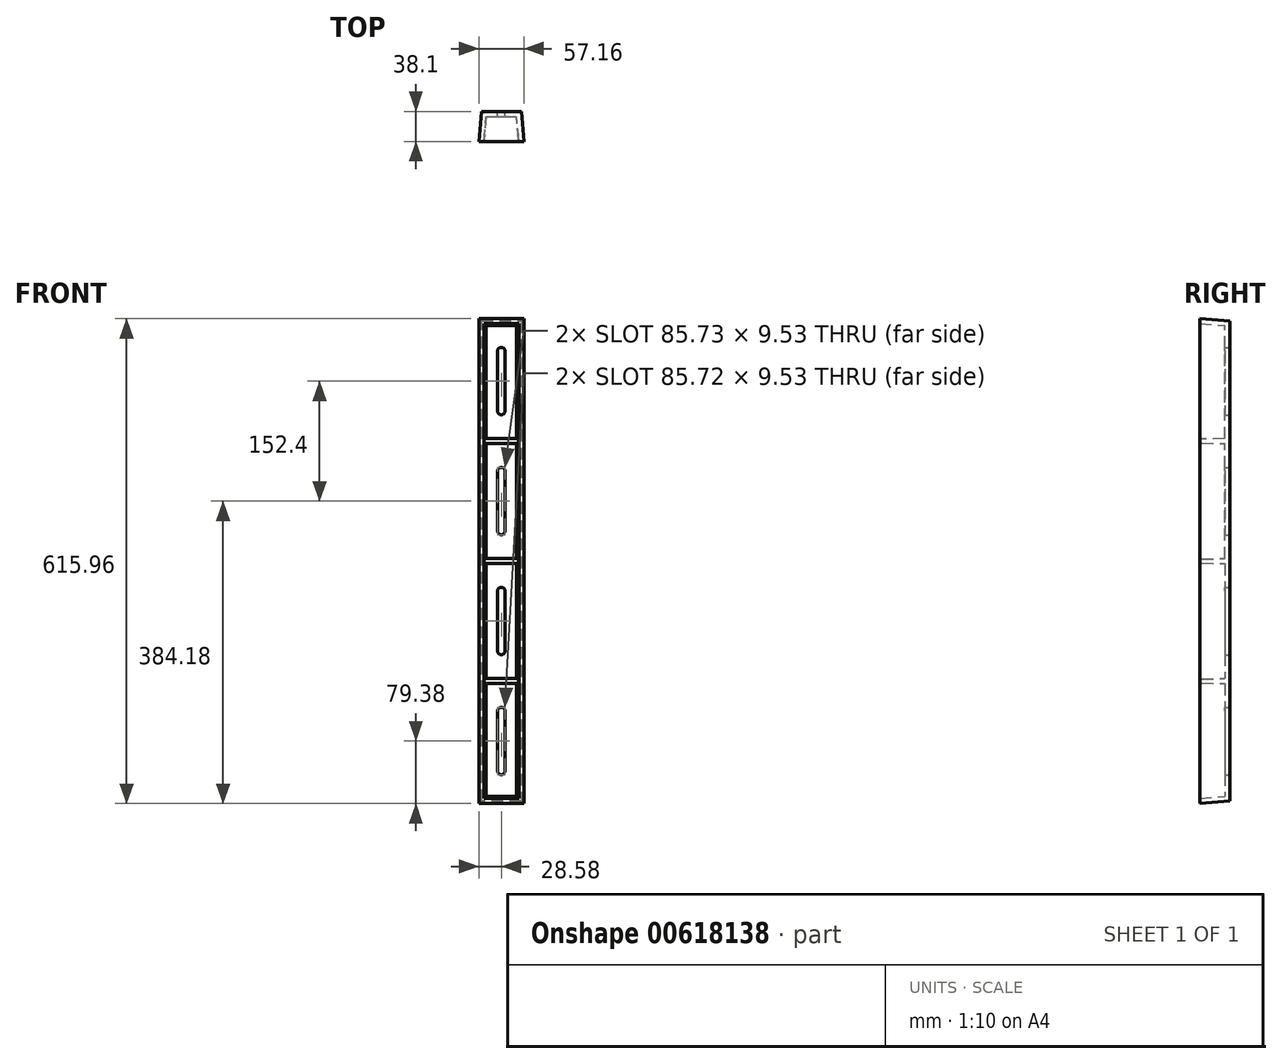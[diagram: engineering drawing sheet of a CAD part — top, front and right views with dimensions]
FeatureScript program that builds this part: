
annotation { "Feature Type Name" : "Feature", "Feature Type Description" : "" }
export const myFeature = defineFeature(function(context is Context, id is Id, definition is map)
    precondition{}
    {
        {
            var Q0;
            Q0=qCreatedBy(makeId("Front.planeOp"),FACE);
            var sketch = newSketch(context, id + "F0", { "sketchPlane" : qUnion([Q0])});
            skLineSegment(sketch, "E0.bottom", {"start": v(0, 0) * mm, "end": v(50.8, 0) * mm});
            skLineSegment(sketch, "E0.top", {"start": v(0, 609.6) * mm, "end": v(50.8, 609.6) * mm});
            skLineSegment(sketch, "E0.left", {"start": v(0, 0) * mm, "end": v(0, 609.6) * mm});
            skLineSegment(sketch, "E0.right", {"start": v(50.8, 0) * mm, "end": v(50.8, 609.6) * mm});
            skSolve(sketch);
        }
        {
            var Q0;
            Q0=qSketchRegion(id+"F0",true);
            extrude(context, id + "F1", {"entities" : qUnion([Q0]), "depth" : 38.1 * mm, "hasDraft" : true, "draftAngle" : 4.76 * degree});
        }
        {
            var Q0;
            Q0=makeQuery(id+"F1.opExtrude","CAP_FACE",FACE,{"disambiguationData":[OSD([sQuery(id+"F0.wireOp",EDGE,"E0.bottom"),sQuery(id+"F0.wireOp",EDGE,"E0.top"),sQuery(id+"F0.wireOp",EDGE,"E0.left"),sQuery(id+"F0.wireOp",EDGE,"E0.right")])],"isStart":false});
            shell(context, id + "F2", {"entities" : qUnion([Q0]), "thickness" : 6.35 * mm});
        }
        {
            var Q0;
            Q0=makeQuery(id+"F1.opExtrude","CAP_FACE",FACE,{"disambiguationData":[OSD([sQuery(id+"F0.wireOp",EDGE,"E0.bottom"),sQuery(id+"F0.wireOp",EDGE,"E0.top"),sQuery(id+"F0.wireOp",EDGE,"E0.left"),sQuery(id+"F0.wireOp",EDGE,"E0.right")])],"isStart":true});
            var sketch = newSketch(context, id + "F3", { "sketchPlane" : qUnion([Q0])});
            skLineSegment(sketch, "E1", {"start": v(-25.4, 0) * mm, "end": v(-25.4, 152.4) * mm, "construction": true});
            skLineSegment(sketch, "E2", {"start": v(-25.4, 152.4) * mm, "end": v(-25.4, 304.8) * mm, "construction": true});
            skLineSegment(sketch, "E3", {"start": v(-25.4, 304.8) * mm, "end": v(-25.4, 457.2) * mm, "construction": true});
            skLineSegment(sketch, "E4", {"start": v(-25.4, 457.2) * mm, "end": v(-25.4, 609.6) * mm, "construction": true});
            skSolve(sketch);
        }
        {
            var Q0;
            Q0=makeQuery(id+"F1.opExtrude","CAP_EDGE",EDGE,{"disambiguationData":[OSD([sQuery(id+"F0.wireOp",EDGE,"E0.bottom")])],"isStart":true});
            cPoint(context, id + "F4", {"entities" : qUnion([Q0]), "parameter" : 0.5});
        }
        {
            var Q0;
            Q0=makeQuery(id+"F1.opExtrude","CAP_EDGE",EDGE,{"disambiguationData":[OSD([sQuery(id+"F0.wireOp",EDGE,"E0.bottom")])],"isStart":false});
            cPoint(context, id + "F5", {"entities" : qUnion([Q0]), "parameter" : 0.5});
        }
        {
            var Q0;
            {var subQ0=sQuery(id+"F0.wireOp",EDGE,"E0.top");Q0=makeQuery(id+"F2.opShell","OFFSET_EDGE",EDGE,{"disambiguationData":[OSD([subQ0]),TDD([makeQuery(id+"F1.opExtrude","CAP_EDGE",EDGE,{"disambiguationData":[OSD([subQ0])],"isStart":false})])]});}
            cPoint(context, id + "F6", {"entities" : qUnion([Q0]), "parameter" : 0.5});
        }
        {
            var Q0;
            Q0=qCreatedBy(id+"F4",VERTEX);
            var Q1;
            Q1=qCreatedBy(id+"F5",VERTEX);
            var Q2;
            Q2=qCreatedBy(id+"F6",VERTEX);
            cPlane(context, id + "F7", {"entities" : qUnion([Q0, Q1, Q2]), "cplaneType" : CPlaneType.THREE_POINT, "offset" : 25.4 * mm, "width" : 152.4 * mm, "height" : 152.4 * mm});
        }
        {
            var Q0;
            Q0=qCreatedBy(id+"F7.planeOp",FACE);
            var sketch = newSketch(context, id + "F8", { "sketchPlane" : qUnion([Q0])});
            skLineSegment(sketch, "E5", {"start": v(-6.35, 603.76) * mm, "end": v(-6.35, 5.84) * mm});
            skLineSegment(sketch, "E6.0", {"start": v(0, 152.4) * mm, "end": v(0, 304.8) * mm, "construction": true});
            skLineSegment(sketch, "E7.0", {"start": v(0, 0) * mm, "end": v(0, 152.4) * mm});
            skLineSegment(sketch, "E8.0", {"start": v(0, 304.8) * mm, "end": v(0, 457.2) * mm, "construction": true});
            skLineSegment(sketch, "E9.0", {"start": v(0, 457.2) * mm, "end": v(0, 609.6) * mm, "construction": true});
            skLineSegment(sketch, "E10.0.0", {"start": v(-6.35, 5.84) * mm, "end": v(-6.35, 603.76) * mm});
            skLineSegment(sketch, "E10.0.1", {"start": v(-6.35, 603.76) * mm, "end": v(-38.1, 606.4) * mm});
            skLineSegment(sketch, "E10.0.2", {"start": v(-38.1, 606.4) * mm, "end": v(-38.1, 3.2) * mm, "construction": true});
            skLineSegment(sketch, "E10.0.3", {"start": v(-38.1, 3.2) * mm, "end": v(-6.35, 5.84) * mm});
            skLineSegment(sketch, "E11", {"start": v(0, 152.4) * mm, "end": v(-38.1, 152.4) * mm, "construction": true});
            skLineSegment(sketch, "E12", {"start": v(0, 304.8) * mm, "end": v(-38.1, 304.8) * mm, "construction": true});
            skLineSegment(sketch, "E13", {"start": v(0, 457.2) * mm, "end": v(-38.1, 457.2) * mm, "construction": true});
            skLineSegment(sketch, "E14.0", {"start": v(0, 155.58) * mm, "end": v(-6.35, 155.58) * mm, "construction": true});
            skLineSegment(sketch, "E15.0", {"start": v(0, 149.22) * mm, "end": v(-6.35, 149.22) * mm, "construction": true});
            skLineSegment(sketch, "E16.0", {"start": v(0, 301.63) * mm, "end": v(-6.35, 301.63) * mm, "construction": true});
            skLineSegment(sketch, "E17.0", {"start": v(0, 307.98) * mm, "end": v(-6.35, 307.98) * mm, "construction": true});
            skLineSegment(sketch, "E18.0", {"start": v(0, 460.38) * mm, "end": v(-6.35, 460.38) * mm, "construction": true});
            skLineSegment(sketch, "E19.0", {"start": v(0, 454.03) * mm, "end": v(-6.35, 454.03) * mm, "construction": true});
            skArc(sketch, "E20", {"start": v(-35.78, 154.78) * mm, "mid": v(-38.1, 152.4) * mm, "end": v(-35.78, 150.02) * mm});
            skArc(sketch, "E21", {"start": v(-35.78, 307.18) * mm, "mid": v(-38.1, 304.8) * mm, "end": v(-35.78, 302.42) * mm});
            skArc(sketch, "E22", {"start": v(-35.78, 459.58) * mm, "mid": v(-38.1, 457.2) * mm, "end": v(-35.78, 454.82) * mm});
            skLineSegment(sketch, "E23", {"start": v(-6.35, 149.22) * mm, "end": v(-35.78, 150.02) * mm});
            skLineSegment(sketch, "E24", {"start": v(-6.35, 155.57) * mm, "end": v(-35.78, 154.78) * mm});
            skLineSegment(sketch, "E25", {"start": v(-6.35, 301.63) * mm, "end": v(-35.78, 302.42) * mm});
            skLineSegment(sketch, "E26", {"start": v(-6.35, 307.98) * mm, "end": v(-35.78, 307.18) * mm});
            skLineSegment(sketch, "E27", {"start": v(-6.35, 454.03) * mm, "end": v(-35.78, 454.82) * mm});
            skLineSegment(sketch, "E28", {"start": v(-6.35, 460.38) * mm, "end": v(-35.78, 459.58) * mm});
            skSolve(sketch);
        }
        {
            var Q0;
            Q0=qSketchRegion(id+"F8",true);
            var Q1;
            Q1=makeQuery(id+"F2.opShell","OFFSET_FACE",FACE,{"disambiguationData":[OSD([sQuery(id+"F0.wireOp",EDGE,"E0.left")])]});
            var Q2;
            Q2=makeQuery(id+"F2.opShell","OFFSET_FACE",FACE,{"disambiguationData":[OSD([sQuery(id+"F0.wireOp",EDGE,"E0.right")])]});
            extrude(context, id + "F9", {"entities" : qUnion([Q0]), "operationType" : NewBodyOperationType.ADD, "endBound" : BoundingType.UP_TO_SURFACE, "oppositeDirection" : true, "endBoundEntityFace" : qUnion([Q1]), "depth" : 25.4 * mm, "hasSecondDirection" : true, "secondDirectionBound" : SecondDirectionBoundingType.UP_TO_SURFACE, "secondDirectionOppositeDirection" : false, "secondDirectionBoundEntityFace" : qUnion([Q2]), "secondDirectionDepth" : 25.4 * mm});
        }
        {
            var Q0;
            Q0=makeQuery(id+"F3.imprint","IMPRINT",FACE,{"disambiguationData":[TD([[makeQuery(id+"F3.imprint","IMPRINT",EDGE,{"derivedFrom":makeQuery(id+"F1.opExtrude","CAP_EDGE",EDGE,{"disambiguationData":[OSD([sQuery(id+"F0.wireOp",EDGE,"E0.bottom")])],"isStart":true})}),-1.0]])]});
            var sketch = newSketch(context, id + "F10", { "sketchPlane" : qUnion([Q0])});
            skLineSegment(sketch, "E29.0", {"start": v(-25.4, 457.2) * mm, "end": v(-25.4, 609.6) * mm, "construction": true});
            skLineSegment(sketch, "E30.0", {"start": v(-25.4, 304.8) * mm, "end": v(-25.4, 457.2) * mm, "construction": true});
            skLineSegment(sketch, "E31.0", {"start": v(-25.4, 152.4) * mm, "end": v(-25.4, 304.8) * mm, "construction": true});
            skLineSegment(sketch, "E32.0", {"start": v(-25.4, 0) * mm, "end": v(-25.4, 152.4) * mm, "construction": true});
            skLineSegment(sketch, "E33.bottom", {"start": v(-30.16, 495.3) * mm, "end": v(-20.64, 495.3) * mm});
            skLineSegment(sketch, "E33.top", {"start": v(-30.16, 571.5) * mm, "end": v(-20.64, 571.5) * mm});
            skLineSegment(sketch, "E33.left", {"start": v(-30.16, 495.3) * mm, "end": v(-30.16, 571.5) * mm});
            skLineSegment(sketch, "E33.right", {"start": v(-20.64, 495.3) * mm, "end": v(-20.64, 571.5) * mm});
            skPoint(sketch, "E33.middle", {"position": v(-25.4, 533.4) * mm});
            skLineSegment(sketch, "E34.bottom", {"start": v(-30.16, 342.9) * mm, "end": v(-20.64, 342.9) * mm});
            skLineSegment(sketch, "E34.top", {"start": v(-30.16, 419.1) * mm, "end": v(-20.64, 419.1) * mm});
            skLineSegment(sketch, "E34.left", {"start": v(-30.16, 342.9) * mm, "end": v(-30.16, 419.1) * mm});
            skLineSegment(sketch, "E34.right", {"start": v(-20.64, 342.9) * mm, "end": v(-20.64, 419.1) * mm});
            skPoint(sketch, "E34.middle", {"position": v(-25.4, 381) * mm});
            skLineSegment(sketch, "E35.bottom", {"start": v(-30.16, 190.5) * mm, "end": v(-20.64, 190.5) * mm});
            skLineSegment(sketch, "E35.top", {"start": v(-30.16, 266.7) * mm, "end": v(-20.64, 266.7) * mm});
            skLineSegment(sketch, "E35.left", {"start": v(-30.16, 190.5) * mm, "end": v(-30.16, 266.7) * mm});
            skLineSegment(sketch, "E35.right", {"start": v(-20.64, 190.5) * mm, "end": v(-20.64, 266.7) * mm});
            skPoint(sketch, "E35.middle", {"position": v(-25.4, 228.6) * mm});
            skLineSegment(sketch, "E36.bottom", {"start": v(-30.16, 38.1) * mm, "end": v(-20.64, 38.1) * mm});
            skLineSegment(sketch, "E36.top", {"start": v(-30.16, 114.3) * mm, "end": v(-20.64, 114.3) * mm});
            skLineSegment(sketch, "E36.left", {"start": v(-30.16, 38.1) * mm, "end": v(-30.16, 114.3) * mm});
            skLineSegment(sketch, "E36.right", {"start": v(-20.64, 38.1) * mm, "end": v(-20.64, 114.3) * mm});
            skPoint(sketch, "E36.middle", {"position": v(-25.4, 76.2) * mm});
            skCircle(sketch, "E37", {"center": v(-25.4, 571.5) * mm, "radius": 4.76 * mm});
            skCircle(sketch, "E38", {"center": v(-25.4, 495.3) * mm, "radius": 4.76 * mm});
            skCircle(sketch, "E39", {"center": v(-25.4, 419.1) * mm, "radius": 4.76 * mm});
            skCircle(sketch, "E40", {"center": v(-25.4, 266.7) * mm, "radius": 4.76 * mm});
            skCircle(sketch, "E41", {"center": v(-25.4, 190.5) * mm, "radius": 4.76 * mm});
            skCircle(sketch, "E42", {"center": v(-25.4, 114.3) * mm, "radius": 4.76 * mm});
            skCircle(sketch, "E43", {"center": v(-25.4, 38.1) * mm, "radius": 4.76 * mm});
            skCircle(sketch, "E44", {"center": v(-25.4, 342.9) * mm, "radius": 4.76 * mm});
            skSolve(sketch);
        }
        {
            var Q0;
            Q0=qSketchRegion(id+"F10",true);
            extrude(context, id + "F11", {"entities" : qUnion([Q0]), "operationType" : NewBodyOperationType.REMOVE, "endBound" : BoundingType.THROUGH_ALL, "oppositeDirection" : true, "depth" : 25.4 * mm});
        }
    });
